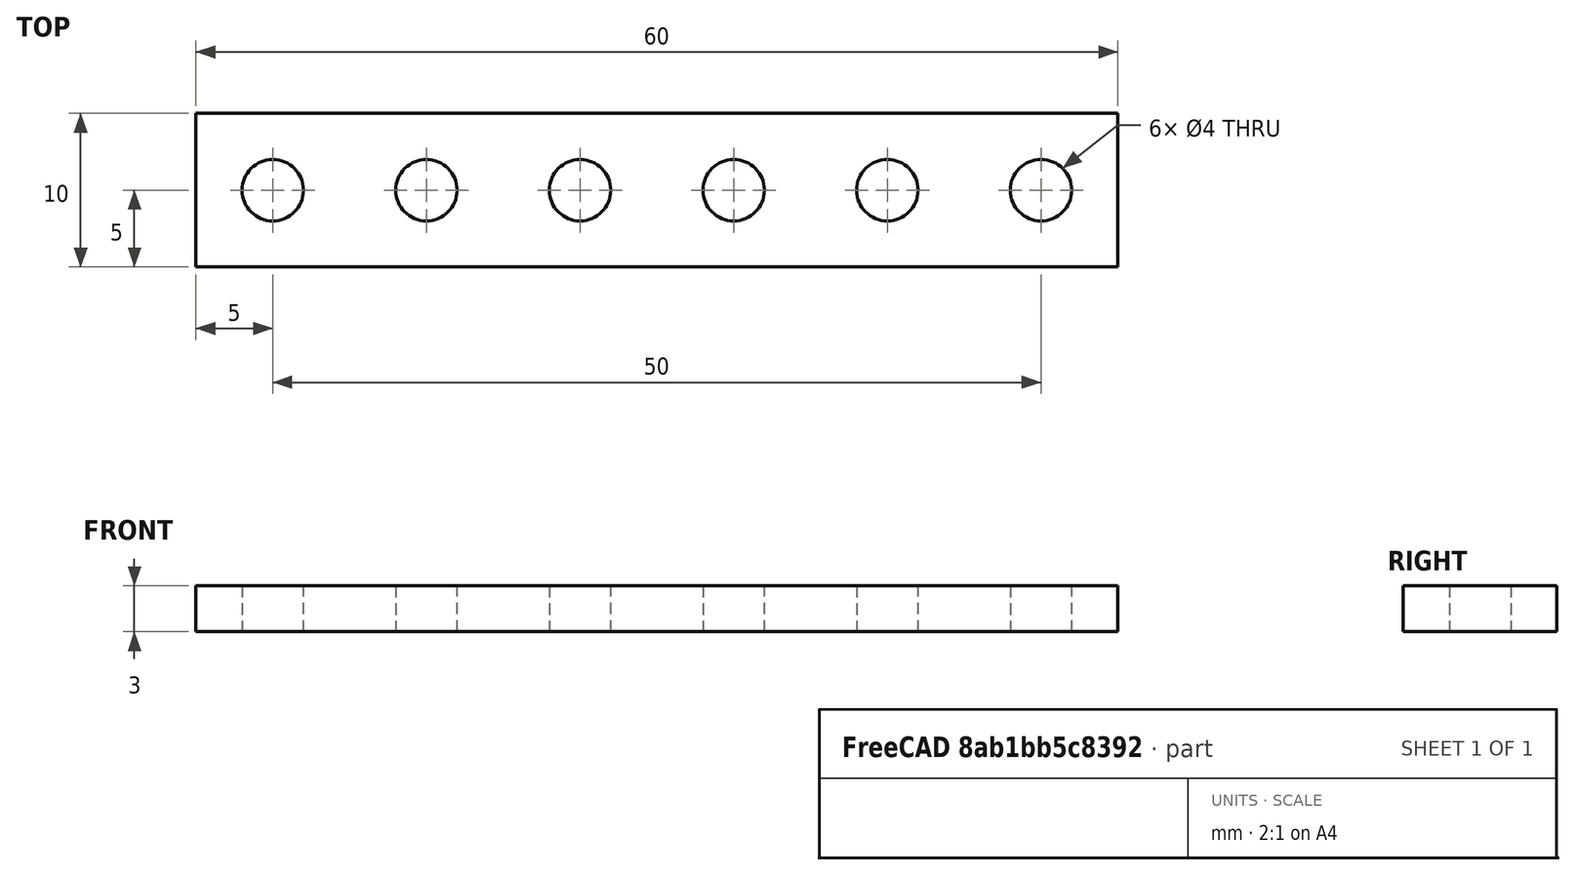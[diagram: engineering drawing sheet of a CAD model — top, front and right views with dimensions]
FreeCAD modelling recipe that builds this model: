
FCSTD DOCUMENT  (FreeCAD 0.17R13217 (Git))
Label: 01-1-pieza-mecano
License: All rights reserved
LicenseURL: http://en.wikipedia.org/wiki/All_rights_reserved
objects: TechDraw::DrawViewDimension×6, TechDraw::DrawProjGroupItem×2, Sketcher::SketchObject×1, PartDesign::Pad×1, PartDesign::Body×1, TechDraw::DrawSVGTemplate×1, TechDraw::DrawProjGroup×1, TechDraw::DrawViewAnnotation×1, TechDraw::DrawViewPart×1, TechDraw::DrawPage×1
note: 4 computed .brp shape members not serialized (recipe doc carries the construction recipe); baked Part::Feature solids carry a one-line shape summary decoded from their .brp

FEATURE [Sketcher::SketchObject] Sketch
  MapMode = 5
  Support = -> [XY_Plane]
  sketch-geometry (14):
    g0: LineSegment StartX=-30 StartY=5 StartZ=0 EndX=30 EndY=5 EndZ=0
    g1: LineSegment StartX=30 StartY=5 StartZ=0 EndX=30 EndY=-5 EndZ=0
    g2: LineSegment StartX=30 StartY=-5 StartZ=0 EndX=-30 EndY=-5 EndZ=0
    g3: LineSegment StartX=-30 StartY=-5 StartZ=0 EndX=-30 EndY=5 EndZ=0
    g4: Circle CenterX=-25 CenterY=0 CenterZ=0 NormalX=0 NormalY=0 NormalZ=1 AngleXU=0 Radius=2
    g5: Circle CenterX=-15 CenterY=0 CenterZ=0 NormalX=0 NormalY=0 NormalZ=1 AngleXU=0 Radius=2
    g6: Circle CenterX=-5 CenterY=0 CenterZ=0 NormalX=0 NormalY=0 NormalZ=1 AngleXU=0 Radius=2
    g7: Circle CenterX=5 CenterY=0 CenterZ=0 NormalX=0 NormalY=0 NormalZ=1 AngleXU=0 Radius=2
    g8: Circle CenterX=15 CenterY=0 CenterZ=0 NormalX=0 NormalY=0 NormalZ=1 AngleXU=0 Radius=2
    g9: Circle CenterX=25 CenterY=0 CenterZ=0 NormalX=0 NormalY=0 NormalZ=1 AngleXU=0 Radius=2
    g10: LineSegment [constr] StartX=-5 StartY=0 StartZ=0 EndX=5 EndY=0 EndZ=0
    g11: LineSegment [constr] StartX=-15 StartY=0 StartZ=0 EndX=-5 EndY=0 EndZ=0
    g12: LineSegment [constr] StartX=-25 StartY=0 StartZ=0 EndX=-15 EndY=0 EndZ=0
    g13: LineSegment [constr] StartX=-25 StartY=0 StartZ=0 EndX=-30 EndY=0 EndZ=0
  constraints (35):
    c: Coincident(g0,g1)
    c: Coincident(g1,g2)
    c: Coincident(g2,g3)
    c: Coincident(g3,g0)
    c: Horizontal(g0)
    c: Horizontal(g2)
    c: Vertical(g1)
    c: Vertical(g3)
    c: Symmetric(g0,g1,g-1)
    c: PointOnObject(g4,g-1)
    c: PointOnObject(g5,g-1)
    c: PointOnObject(g6,g-1)
    c: Equal(g4,g5)
    c: Equal(g5,g6)
    c: Equal(g6,g7)
    c: Equal(g7,g8)
    c: Equal(g8,g9)
    c: Symmetric(g6,g7,g-2)
    c: Coincident(g10,g6)
    c: Coincident(g10,g7)
    c: DistanceX(g10,g10) = 10  'a'
    c: Coincident(g11,g5)
    c: Coincident(g11,g6)
    c: Coincident(g12,g4)
    c: Coincident(g12,g5)
    c: Symmetric(g5,g8,g-2)
    c: Symmetric(g4,g9,g-2)
    c: Equal(g11,g10)
    c: Equal(g10,g12)
    c: Coincident(g13,g4)
    c: PointOnObject(g13,g3)
    c: Horizontal(g13)
    c: DistanceX(g13,g13) = 5
    c: Radius(g9) = 2
    c: DistanceY(g1,g1) = 10
FEATURE [PartDesign::Pad] Pad
  Length = 3
  Length2 = 100
  Profile = -> Sketch
  Refine = true
  Type = 0
FEATURE [PartDesign::Body] Body  label="Pieza-mecano"
  Group = -> [Sketch,Pad]
  Origin = -> Origin
  Tip = -> Pad
FEATURE [TechDraw::DrawSVGTemplate] Template
  EditableTexts = Designed_by_Name=Designed by Name; Drawing_number=Drawing number; FC-Date=Date; FC-SC=Scale; FC-SH=Sheet; FC-Title=Title; Subtitle=Subtitle; Weight=Weight
  Height = 210
  Orientation = 1
  Width = 297
FEATURE [TechDraw::DrawProjGroupItem] ProjItem  label="Front"
  ArcCenterMarks = true
  CenterScale = 2
  CoarseView = false
  Direction = (0,-1,0)
  ExtraWidth = 1.4
  Focus = 100
  HardHidden = false
  HiddenWidth = 0.35
  HorizCenterLine = false
  IsoCount = 0
  IsoHidden = false
  IsoVisible = false
  IsoWidth = 0.5
  KeepLabel = false
  LineWidth = 0.7
  LockPosition = false
  Perspective = false
  Rotation = 0
  RotationVector = (1,0,0)
  ScaleType = 0
  SeamHidden = false
  SeamVisible = false
  ShowSectionLine = true
  SmoothHidden = false
  SmoothVisible = false
  Source = -> [Pad]
  Type = 0
  VertCenterLine = false
  X = 0
  Y = 0
FEATURE [TechDraw::DrawProjGroupItem] ProjItem001  label="Bottom"
  ArcCenterMarks = true
  CenterScale = 2
  CoarseView = false
  Direction = (0,0,-1)
  ExtraWidth = 1.4
  Focus = 100
  HardHidden = false
  HiddenWidth = 0.35
  HorizCenterLine = false
  IsoCount = 0
  IsoHidden = false
  IsoVisible = false
  IsoWidth = 0.5
  KeepLabel = false
  LineWidth = 0.7
  LockPosition = false
  Perspective = false
  Rotation = 0
  RotationVector = (1,0,0)
  ScaleType = 0
  SeamHidden = false
  SeamVisible = false
  ShowSectionLine = true
  SmoothHidden = false
  SmoothVisible = false
  Source = -> [Pad]
  Type = 5
  VertCenterLine = false
  X = -1.39584
  Y = 60.3754
FEATURE [TechDraw::DrawProjGroup] ProjGroup
  Anchor = -> ProjItem
  AutoDistribute = false
  CubeDirs = (1) [(0,0,0)]
  CubeRotations = (1) [(0,0,0)]
  KeepLabel = false
  LockPosition = false
  ProjectionType = 0
  Rotation = 0
  ScaleType = 0
  Source = -> [Pad]
  Views = -> [ProjItem,ProjItem001]
  X = 72.8008
  Y = 86.394
  spacingX = 17
  spacingY = 15
FEATURE [TechDraw::DrawViewDimension] Dimension
  Font = osifont
  Fontsize = 3.5
  FormatSpec = %.2f
  KeepLabel = false
  LineWidth = 0.5
  LockPosition = false
  MeasureType = 1
  References2D = -> [ProjItem001]
  Rotation = 0
  ScaleType = 0
  Type = 1
  X = -3.03495
  Y = -29.9198
FEATURE [TechDraw::DrawViewDimension] Dimension001
  Caption = hola
  Font = osifont
  Fontsize = 4.5
  FormatSpec = %0f
  KeepLabel = false
  LineWidth = 0.5
  LockPosition = false
  MeasureType = 1
  References2D = -> [ProjItem001]
  Rotation = 0
  ScaleType = 0
  Type = 2
  X = 42.2585
  Y = -24.0334
FEATURE [TechDraw::DrawViewDimension] Dimension002
  Font = osifont
  Fontsize = 3.5
  FormatSpec = %.1f
  KeepLabel = false
  LineWidth = 0.5
  LockPosition = false
  MeasureType = 1
  References2D = -> [ProjItem001]
  Rotation = 0
  ScaleType = 0
  Type = 5
  X = 49.4155
  Y = 17.1242
FEATURE [TechDraw::DrawViewDimension] Dimension003
  Font = osifont
  Fontsize = 3.5
  FormatSpec = %.2f
  KeepLabel = false
  LineWidth = 0.5
  LockPosition = false
  MeasureType = 1
  References2D = -> [ProjItem]
  Rotation = 0
  ScaleType = 0
  Type = 2
  X = 40.5995
  Y = 24.0031
FEATURE [TechDraw::DrawViewDimension] Dimension004
  Font = osifont
  Fontsize = 3.5
  FormatSpec = %.2f
  KeepLabel = false
  LineWidth = 0.5
  LockPosition = false
  MeasureType = 1
  References2D = -> [ProjItem001]
  Rotation = 0
  ScaleType = 0
  Type = 1
  X = 13.9311
  Y = -20.2751
FEATURE [TechDraw::DrawViewDimension] Dimension005
  Font = osifont
  Fontsize = 3.5
  FormatSpec = %.2f
  KeepLabel = false
  LineWidth = 0.5
  LockPosition = false
  MeasureType = 1
  References2D = -> [ProjItem001]
  Rotation = 0
  ScaleType = 0
  Type = 1
  X = -7.70247
  Y = 14.977
FEATURE [TechDraw::DrawViewAnnotation] Annotation
  Font = osifont
  KeepLabel = false
  LineSpace = 80
  LockPosition = false
  MaxWidth = -1
  Rotation = 0
  ScaleType = 0
  Text = Pieza mecano
  TextSize = 8
  TextStyle = 0
  X = 199.969
  Y = 163.009
FEATURE [TechDraw::DrawViewPart] View
  ArcCenterMarks = true
  CenterScale = 2
  CoarseView = false
  Direction = (1,1,1)
  ExtraWidth = 1.4
  Focus = 100
  HardHidden = false
  HiddenWidth = 0.35
  HorizCenterLine = false
  IsoCount = 0
  IsoHidden = false
  IsoVisible = false
  IsoWidth = 0.5
  KeepLabel = false
  LineWidth = 0.7
  LockPosition = false
  Perspective = false
  Rotation = 0
  ScaleType = 0
  SeamHidden = false
  SeamVisible = false
  ShowSectionLine = true
  SmoothHidden = false
  SmoothVisible = false
  Source = -> [Pad]
  VertCenterLine = false
  X = 201.87
  Y = 111.033
FEATURE [TechDraw::DrawPage] Page  label="Planos"
  KeepUpdated = true
  ProjectionType = 0
  Template = -> Template
  Views = -> [ProjGroup,Dimension,Dimension001,Dimension002,Dimension003,Dimension004,Dimension005,Annotation,View]
